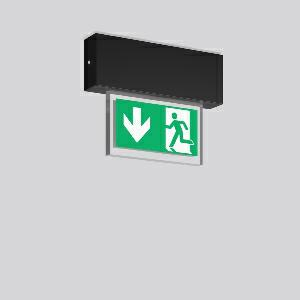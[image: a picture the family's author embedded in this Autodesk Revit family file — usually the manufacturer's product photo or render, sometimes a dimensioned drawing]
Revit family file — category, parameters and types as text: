
# Revit family: halyxx_671504_003_1_89_5388
name_source: partatom
category: Lighting Fixtures
units: mm (PartAtom-declared; Revit-internal decimal feet)

## family parameters
Cut with Voids When Loaded = No
Host = Face
Light Source = No
Part Type = Normal
Room Calculation Point = No
Round Connector Dimension = Use Diameter
Shared = No

## types (1)
- HALYXX (1 x LED Modul 840, 45 lm, 4000)
    Apparent Load = 3 VA
    Approval mark = CE
    CIE Flux Codes = 18 46 75 53 100
    Color Rendering = 80
    Color Temperature = 4000
    Default Elevation = 1800 mm
    Description = Series: HALYXX
Luminaire for escape route identification. Housing: extruded aluminium profile, anodised or powder-coated. Display panel: highly transparent panel, plastic, with legend on one side/both sides. Driver integrated. Suitable for connection to central battery systems. With AC Control monitoring module for LUXIFAIR central battery units. Please indicate legend number when placing your order! 
Colour: black
Length: 233 mm
Width: 40 mm
Height: 184 mm
Weight: 1.03 kg
Operating mode: maintained power mode
Viewing Distance: 14 m
Lamp: LED
Socket: without socket
Colour temperature: 4000K
Colour rendering index (CRI): 80
System power: 3 W
Rated luminous flux: 45 lm
Luminous flux, emergency: 45
System power, emergency: 2.8 W
Control gear: Regulated power supply
Protection class: I
Type of protection: IP 40
    Height = 184 mm
    Lamp = 1 x LED Modul 840
    Lamp Light Flux = 45 lm
    Lamp count = 1
    Length = 233 mm
    Lifetime = 50000 h
    Luminous efficacy = 15 lm/W
    Manufacturer = RZB
    ModVariant = No
    Model = 671504.003.1.89
    Mounting Place = Ceiling
    Mounting Type = Surface mounted
    Number of Poles = 1
    OnlyDefault = Yes
    Power Factor = 1
    Product Name = HALYXX
    Product group = Surface mounted ceiling luminaires
    ProductGroupID = 303
    Protection Class = Protection class I
    Protection Degree = IP 40
    RLX_Detail_Level = 1
    RLX_Emergency_Light_Flux = 45 lm
    RLX_Emergency_Type = 3
    RLX_Emergency_Type_DB = Yes
    RlxData = <blob elided: 35013 chars, md5=d7b194f5>
    Socket = socket
    Standby Power = 0 W
    System Light Flux = 45 lm
    System Power = 3 W
    Type Comments = Product without accessories
    Type Image = 671502.003.jpg
    URL = http://relux.com
    VarID = ---
    Voltage = 230 V
    Voltage Range = 220-240 V
    Weight = 0.00 kg
    Width = 40 mm  [stored 0.131234 ft]

note: [stored X ft] marks values corroborated as IEEE doubles in the binary element streams (Revit-internal decimal feet)

## geometry (parser evidence)
native form markers: Blend x4, Sweep x14
no freeform markers — native parametric forms only
